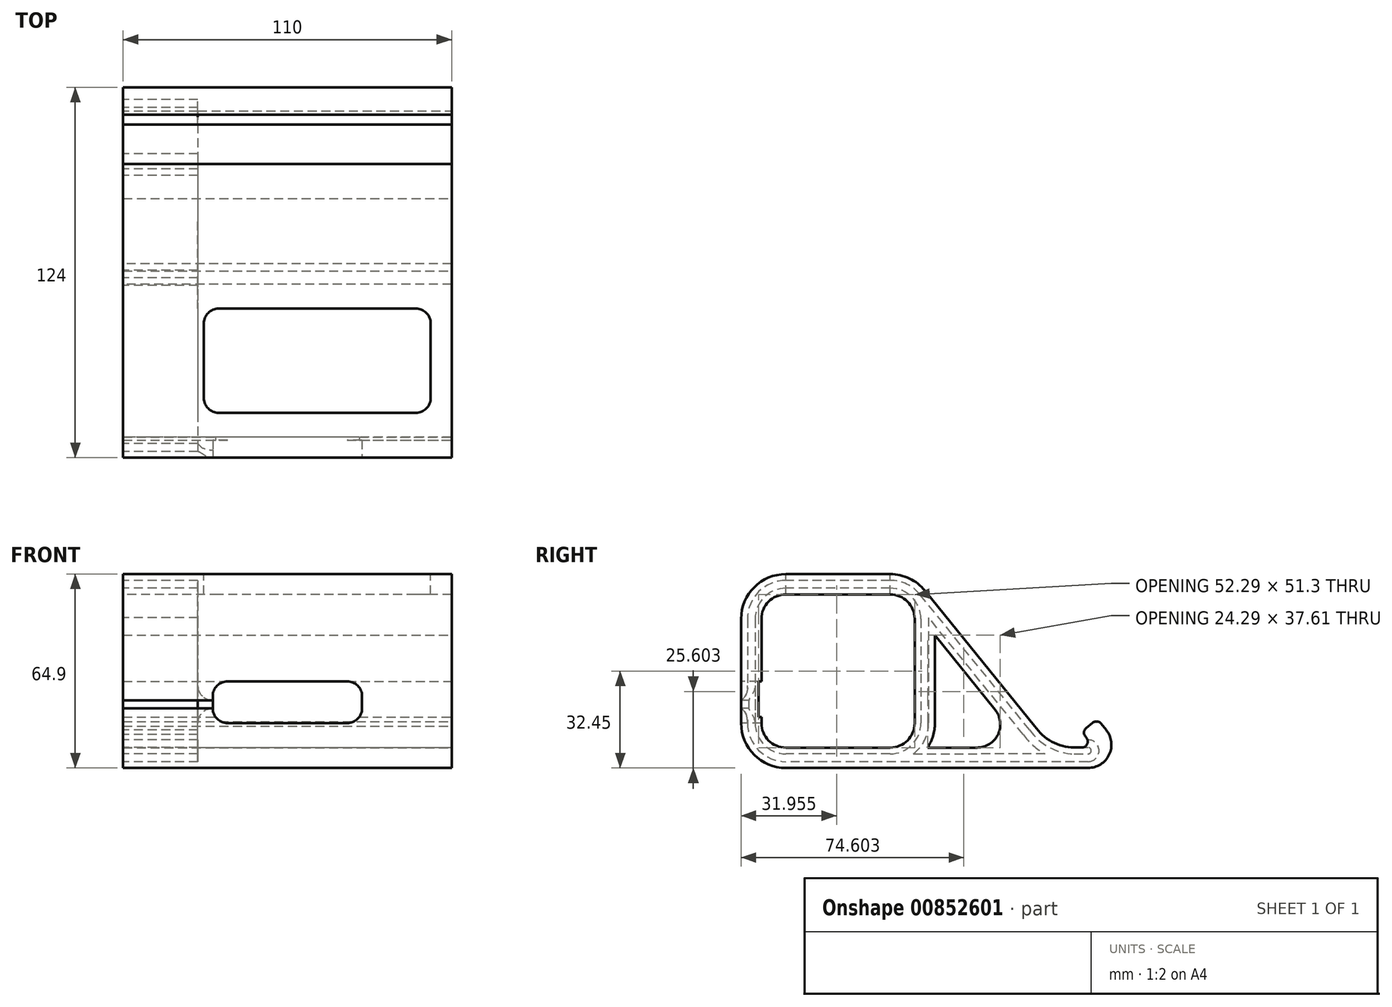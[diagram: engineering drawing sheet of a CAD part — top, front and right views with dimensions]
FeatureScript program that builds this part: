
annotation { "Feature Type Name" : "Feature", "Feature Type Description" : "" }
export const myFeature = defineFeature(function(context is Context, id is Id, definition is map)
    precondition{}
    {
        {
            var Q0;
            Q0=qCreatedBy(makeId("Right.planeOp"),FACE);
            var sketch = newSketch(context, id + "F0", { "sketchPlane" : qUnion([Q0])});
            skPoint(sketch, "E0.middle", {"position": v(0, 0) * mm});
            skArc(sketch, "E1.0", {"start": v(25.65, 17.45) * mm, "mid": v(23.25, 23.25) * mm, "end": v(17.45, 25.65) * mm});
            skLineSegment(sketch, "E1.1", {"start": v(25.65, 17.45) * mm, "end": v(25.65, -17.45) * mm});
            skLineSegment(sketch, "E1.2", {"start": v(17.45, 25.65) * mm, "end": v(-17.45, 25.65) * mm});
            skArc(sketch, "E1.3", {"start": v(17.45, -25.65) * mm, "mid": v(23.25, -23.25) * mm, "end": v(25.65, -17.45) * mm});
            skArc(sketch, "E1.4", {"start": v(-17.45, 25.65) * mm, "mid": v(-23.25, 23.25) * mm, "end": v(-25.65, 17.45) * mm});
            skLineSegment(sketch, "E1.5", {"start": v(-25.65, 17.45) * mm, "end": v(-25.65, -17.45) * mm});
            skArc(sketch, "E1.6", {"start": v(-25.65, -17.45) * mm, "mid": v(-23.25, -23.25) * mm, "end": v(-17.45, -25.65) * mm});
            skLineSegment(sketch, "E1.7", {"start": v(17.45, -25.65) * mm, "end": v(-17.45, -25.65) * mm});
            skLineSegment(sketch, "E2.0", {"start": v(-32.45, 17.45) * mm, "end": v(-32.45, -17.45) * mm});
            skArc(sketch, "E2.1", {"start": v(-17.45, 32.45) * mm, "mid": v(-28.06, 28.06) * mm, "end": v(-32.45, 17.45) * mm});
            skArc(sketch, "E2.2", {"start": v(-32.45, -17.45) * mm, "mid": v(-28.06, -28.06) * mm, "end": v(-17.45, -32.45) * mm});
            skLineSegment(sketch, "E2.3", {"start": v(17.45, 32.45) * mm, "end": v(-17.45, 32.45) * mm});
            skLineSegment(sketch, "E2.4", {"start": v(17.45, -32.45) * mm, "end": v(-17.45, -32.45) * mm});
            skArc(sketch, "E2.5", {"start": v(17.45, -32.45) * mm, "mid": v(28.06, -28.06) * mm, "end": v(32.45, -17.45) * mm});
            skLineSegment(sketch, "E2.6", {"start": v(32.45, 17.45) * mm, "end": v(32.45, -17.45) * mm});
            skArc(sketch, "E2.7", {"start": v(32.45, 17.45) * mm, "mid": v(28.06, 28.06) * mm, "end": v(17.45, 32.45) * mm});
            skLineSegment(sketch, "E3.0", {"start": v(17.45, -27.75) * mm, "end": v(-17.45, -27.75) * mm});
            skArc(sketch, "E3.1", {"start": v(-27.75, -17.45) * mm, "mid": v(-24.73, -24.73) * mm, "end": v(-17.45, -27.75) * mm});
            skArc(sketch, "E3.2", {"start": v(17.45, -27.75) * mm, "mid": v(24.73, -24.73) * mm, "end": v(27.75, -17.45) * mm});
            skLineSegment(sketch, "E3.3", {"start": v(-27.75, 17.45) * mm, "end": v(-27.75, -17.45) * mm});
            skLineSegment(sketch, "E3.4", {"start": v(27.75, 17.45) * mm, "end": v(27.75, -17.45) * mm});
            skArc(sketch, "E3.5", {"start": v(27.75, 17.45) * mm, "mid": v(24.73, 24.73) * mm, "end": v(17.45, 27.75) * mm});
            skLineSegment(sketch, "E3.6", {"start": v(17.45, 27.75) * mm, "end": v(-17.45, 27.75) * mm});
            skArc(sketch, "E3.7", {"start": v(-17.45, 27.75) * mm, "mid": v(-24.73, 24.73) * mm, "end": v(-27.75, 17.45) * mm});
            skArc(sketch, "E4.0", {"start": v(30.35, 17.45) * mm, "mid": v(26.57, 26.57) * mm, "end": v(17.45, 30.35) * mm});
            skLineSegment(sketch, "E4.1", {"start": v(30.35, 17.45) * mm, "end": v(30.35, -17.45) * mm});
            skLineSegment(sketch, "E4.2", {"start": v(17.45, 30.35) * mm, "end": v(-17.45, 30.35) * mm});
            skArc(sketch, "E4.3", {"start": v(17.45, -30.35) * mm, "mid": v(26.57, -26.57) * mm, "end": v(30.35, -17.45) * mm});
            skArc(sketch, "E4.4", {"start": v(-17.45, 30.35) * mm, "mid": v(-26.57, 26.57) * mm, "end": v(-30.35, 17.45) * mm});
            skLineSegment(sketch, "E4.5", {"start": v(-30.35, 17.45) * mm, "end": v(-30.35, -17.45) * mm});
            skArc(sketch, "E4.6", {"start": v(-30.35, -17.45) * mm, "mid": v(-26.57, -26.57) * mm, "end": v(-17.45, -30.35) * mm});
            skLineSegment(sketch, "E4.7", {"start": v(17.45, -30.35) * mm, "end": v(-17.45, -30.35) * mm});
            skSolve(sketch);
        }
        {
            var Q0;
            Q0=makeQuery(id+"F0.imprint","IMPRINT",FACE,{"disambiguationData":[TD([[makeQuery(id+"F0.imprint","IMPRINT",EDGE,{"derivedFrom":sQuery(id+"F0.wireOp",EDGE,"E3.0")}),1.0]])]});
            var Q1;
            Q1=makeQuery(id+"F0.imprint","IMPRINT",FACE,{"disambiguationData":[TD([[makeQuery(id+"F0.imprint","IMPRINT",EDGE,{"derivedFrom":sQuery(id+"F0.wireOp",EDGE,"E1.0")}),-1.0]])]});
            var Q2;
            Q2=makeQuery(id+"F0.imprint","IMPRINT",FACE,{"disambiguationData":[TD([[makeQuery(id+"F0.imprint","IMPRINT",EDGE,{"derivedFrom":sQuery(id+"F0.wireOp",EDGE,"E2.0")}),1.0]])]});
            extrude(context, id + "F1", {"entities" : qUnion([Q0, Q1, Q2]), "endBound" : BoundingType.SYMMETRIC, "depth" : 110 * mm, "offsetDistance" : 25 * mm});
        }
        {
            var Q0;
            Q0=makeQuery(id+"F1.opExtrude","SWEPT_FACE",FACE,{"disambiguationData":[OSD([sQuery(id+"F0.wireOp",EDGE,"E2.0")])]});
            var sketch = newSketch(context, id + "F2", { "sketchPlane" : qUnion([Q0])});
            skLineSegment(sketch, "E5", {"start": v(-55, -4.86) * mm, "end": v(-25, -4.86) * mm, "construction": true});
            skLineSegment(sketch, "E6", {"start": v(55, -5.4) * mm, "end": v(25, -5.4) * mm, "construction": true});
            skLineSegment(sketch, "E7", {"start": v(0, -17.45) * mm, "end": v(0, -3.45) * mm, "construction": true});
            skLineSegment(sketch, "E8.bottom", {"start": v(-25, -17.45) * mm, "end": v(25, -17.45) * mm});
            skLineSegment(sketch, "E8.top", {"start": v(-25, -3.45) * mm, "end": v(25, -3.45) * mm});
            skLineSegment(sketch, "E8.left", {"start": v(-25, -17.45) * mm, "end": v(-25, -3.45) * mm});
            skLineSegment(sketch, "E8.right", {"start": v(25, -17.45) * mm, "end": v(25, -3.45) * mm});
            skSolve(sketch);
        }
        {
            var Q0;
            Q0=makeQuery(id+"F2.imprint","IMPRINT",FACE,{"disambiguationData":[TD([[makeQuery(id+"F2.imprint","IMPRINT",EDGE,{"derivedFrom":sQuery(id+"F2.wireOp",EDGE,"E8.bottom")}),-1.0]])]});
            extrude(context, id + "F3", {"entities" : qUnion([Q0]), "operationType" : NewBodyOperationType.REMOVE, "oppositeDirection" : true, "depth" : 7 * mm, "offsetDistance" : 25 * mm});
        }
        {
            var Q0;
            Q0=makeQuery(id+"F1.opExtrude","CAP_FACE",FACE,{"disambiguationData":[OSD([sQuery(id+"F0.wireOp",EDGE,"E1.0"),sQuery(id+"F0.wireOp",EDGE,"E1.1"),sQuery(id+"F0.wireOp",EDGE,"E1.2"),sQuery(id+"F0.wireOp",EDGE,"E1.3"),sQuery(id+"F0.wireOp",EDGE,"E1.4"),sQuery(id+"F0.wireOp",EDGE,"E1.5"),sQuery(id+"F0.wireOp",EDGE,"E1.6"),sQuery(id+"F0.wireOp",EDGE,"E1.7"),sQuery(id+"F0.wireOp",EDGE,"E2.0"),sQuery(id+"F0.wireOp",EDGE,"E2.1"),sQuery(id+"F0.wireOp",EDGE,"E2.2"),sQuery(id+"F0.wireOp",EDGE,"E2.3"),sQuery(id+"F0.wireOp",EDGE,"E2.4"),sQuery(id+"F0.wireOp",EDGE,"E2.5"),sQuery(id+"F0.wireOp",EDGE,"E2.6"),sQuery(id+"F0.wireOp",EDGE,"E2.7")])],"isStart":false});
            var sketch = newSketch(context, id + "F4", { "sketchPlane" : qUnion([Q0])});
            skLineSegment(sketch, "E9", {"start": v(-29.91, -17.45) * mm, "end": v(-25.65, -17.45) * mm, "construction": true});
            skLineSegment(sketch, "E10", {"start": v(-27.78, -17.45) * mm, "end": v(-27.78, -3.45) * mm, "construction": true});
            skLineSegment(sketch, "E11.bottom", {"start": v(-25.64, -3.45) * mm, "end": v(-26.64, -3.45) * mm});
            skLineSegment(sketch, "E11.top", {"start": v(-25.64, -15.45) * mm, "end": v(-26.64, -15.45) * mm});
            skLineSegment(sketch, "E11.left", {"start": v(-25.64, -3.45) * mm, "end": v(-25.64, -15.45) * mm});
            skLineSegment(sketch, "E11.right", {"start": v(-26.64, -3.45) * mm, "end": v(-26.64, -15.45) * mm});
            skSolve(sketch);
        }
        {
            var Q0;
            {var subQ0=sQuery(id+"F4.wireOp",EDGE,"E11.right");Q0=makeQuery(id+"F4.imprint","IMPRINT",FACE,{"disambiguationData":[TD([[makeQuery(id+"F4.imprint","IMPRINT",EDGE,{"derivedFrom":subQ0}),1.0]])]});}
            extrude(context, id + "F5", {"entities" : qUnion([Q0]), "operationType" : NewBodyOperationType.REMOVE, "oppositeDirection" : true, "depth" : 110 * mm, "offsetDistance" : 25 * mm});
        }
        {
            var Q0;
            Q0=makeQuery(id+"F1.opExtrude","CAP_FACE",FACE,{"disambiguationData":[OSD([sQuery(id+"F0.wireOp",EDGE,"E1.0"),sQuery(id+"F0.wireOp",EDGE,"E1.1"),sQuery(id+"F0.wireOp",EDGE,"E1.2"),sQuery(id+"F0.wireOp",EDGE,"E1.3"),sQuery(id+"F0.wireOp",EDGE,"E1.4"),sQuery(id+"F0.wireOp",EDGE,"E1.5"),sQuery(id+"F0.wireOp",EDGE,"E1.6"),sQuery(id+"F0.wireOp",EDGE,"E1.7"),sQuery(id+"F0.wireOp",EDGE,"E2.0"),sQuery(id+"F0.wireOp",EDGE,"E2.1"),sQuery(id+"F0.wireOp",EDGE,"E2.2"),sQuery(id+"F0.wireOp",EDGE,"E2.3"),sQuery(id+"F0.wireOp",EDGE,"E2.4"),sQuery(id+"F0.wireOp",EDGE,"E2.5"),sQuery(id+"F0.wireOp",EDGE,"E2.6"),sQuery(id+"F0.wireOp",EDGE,"E2.7")])],"isStart":false});
            var sketch = newSketch(context, id + "F6", { "sketchPlane" : qUnion([Q0])});
            skLineSegment(sketch, "E12", {"start": v(67.38, -20.37) * mm, "end": v(28.06, 28.19) * mm});
            skPoint(sketch, "E12.endSnap0", {"position": v(28.06, 28.06) * mm});
            skPoint(sketch, "E13.end.orphan", {"position": v(36.97, -25.63) * mm});
            skLineSegment(sketch, "E14", {"start": v(0, -32.45) * mm, "end": v(77.16, -32.45) * mm});
            skLineSegment(sketch, "E15", {"start": v(71.64, -25.63) * mm, "end": v(71.65, -25.65) * mm});
            skLineSegment(sketch, "E16.0", {"start": v(52.61, -12.94) * mm, "end": v(22.77, 23.9) * mm});
            skLineSegment(sketch, "E16.1", {"start": v(0, -25.65) * mm, "end": v(46.55, -25.65) * mm});
            skArc(sketch, "E17.filletArc", {"start": v(46.55, -25.65) * mm, "mid": v(53.6, -21.2) * mm, "end": v(52.61, -12.94) * mm});
            skLineSegment(sketch, "E18", {"start": v(79.1, -25.63) * mm, "end": v(81.64, -25.63) * mm});
            skLineSegment(sketch, "E19", {"start": v(83.2, -22.37) * mm, "end": v(82.81, -21.9) * mm});
            skLineSegment(sketch, "E20", {"start": v(83.1, -19.09) * mm, "end": v(85.28, -17.33) * mm});
            skLineSegment(sketch, "E21", {"start": v(88.1, -17.62) * mm, "end": v(89.81, -19.74) * mm});
            skLineSegment(sketch, "E22", {"start": v(81.35, -32.45) * mm, "end": v(83.75, -32.45) * mm});
            skArc(sketch, "E23.filletArc", {"start": v(83.75, -32.45) * mm, "mid": v(90.79, -28) * mm, "end": v(89.81, -19.74) * mm});
            skPoint(sketch, "E24.visualSharp", {"position": v(86.84, -16.07) * mm});
            skArc(sketch, "E24.filletArc", {"start": v(88.1, -17.62) * mm, "mid": v(86.75, -16.9) * mm, "end": v(85.28, -17.33) * mm});
            skPoint(sketch, "E25.visualSharp", {"position": v(81.55, -20.35) * mm});
            skArc(sketch, "E25.filletArc", {"start": v(83.1, -19.09) * mm, "mid": v(82.38, -20.43) * mm, "end": v(82.81, -21.9) * mm});
            skPoint(sketch, "E26.visualSharp", {"position": v(85.83, -25.63) * mm});
            skArc(sketch, "E26.filletArc", {"start": v(81.64, -25.63) * mm, "mid": v(83.44, -24.5) * mm, "end": v(83.2, -22.37) * mm});
            skLineSegment(sketch, "E27", {"start": v(77.16, -32.45) * mm, "end": v(81.35, -32.45) * mm});
            skArc(sketch, "E28", {"start": v(65.83, -18.46) * mm, "mid": v(71.62, -23.63) * mm, "end": v(79.1, -25.63) * mm});
            skSolve(sketch);
        }
        {
            var Q0;
            {var subQ1=sQuery(id+"F6.wireOp",EDGE,"E17.filletArc");Q0=makeQuery(id+"F6.imprint","IMPRINT",FACE,{"disambiguationData":[TD([[makeQuery(id+"F6.imprint","IMPRINT",EDGE,{"derivedFrom":subQ1}),-1.0]])]});}
            extrude(context, id + "F7", {"entities" : qUnion([Q0]), "oppositeDirection" : true, "depth" : 110 * mm, "offsetDistance" : 25 * mm});
        }
        {
            var Q0;
            Q0=makeQuery(id+"F1.opExtrude","SWEPT_BODY",BODY,{"disambiguationData":[OSD([sQuery(id+"F0.wireOp",EDGE,"E1.0"),sQuery(id+"F0.wireOp",EDGE,"E1.1"),sQuery(id+"F0.wireOp",EDGE,"E1.2"),sQuery(id+"F0.wireOp",EDGE,"E1.3"),sQuery(id+"F0.wireOp",EDGE,"E1.4"),sQuery(id+"F0.wireOp",EDGE,"E1.5"),sQuery(id+"F0.wireOp",EDGE,"E1.6"),sQuery(id+"F0.wireOp",EDGE,"E1.7"),sQuery(id+"F0.wireOp",EDGE,"E2.0"),sQuery(id+"F0.wireOp",EDGE,"E2.1"),sQuery(id+"F0.wireOp",EDGE,"E2.2"),sQuery(id+"F0.wireOp",EDGE,"E2.3"),sQuery(id+"F0.wireOp",EDGE,"E2.4"),sQuery(id+"F0.wireOp",EDGE,"E2.5"),sQuery(id+"F0.wireOp",EDGE,"E2.6"),sQuery(id+"F0.wireOp",EDGE,"E2.7")])]});
            var Q1;
            Q1=makeQuery(id+"F7.opExtrude","SWEPT_BODY",BODY,{"disambiguationData":[OSD([sQuery(id+"F0.wireOp",EDGE,"E2.5"),sQuery(id+"F0.wireOp",EDGE,"E2.6"),sQuery(id+"F0.wireOp",EDGE,"E2.7"),sQuery(id+"F6.wireOp",EDGE,"E12"),sQuery(id+"F6.wireOp",EDGE,"E14"),sQuery(id+"F6.wireOp",EDGE,"E16.0"),sQuery(id+"F6.wireOp",EDGE,"E16.1"),sQuery(id+"F6.wireOp",EDGE,"E17.filletArc"),sQuery(id+"F6.wireOp",EDGE,"E18"),sQuery(id+"F6.wireOp",EDGE,"E19"),sQuery(id+"F6.wireOp",EDGE,"E20"),sQuery(id+"F6.wireOp",EDGE,"E21"),sQuery(id+"F6.wireOp",EDGE,"E22"),sQuery(id+"F6.wireOp",EDGE,"E23.filletArc"),sQuery(id+"F6.wireOp",EDGE,"E24.filletArc"),sQuery(id+"F6.wireOp",EDGE,"E25.filletArc"),sQuery(id+"F6.wireOp",EDGE,"E26.filletArc"),sQuery(id+"F6.wireOp",EDGE,"E27"),sQuery(id+"F6.wireOp",EDGE,"E28")])]});
            booleanBodies(context, id + "F8", {"operationType" : BooleanOperationType.UNION, "tools" : qUnion([Q0, Q1])});
        }
        {
            var Q0;
            Q0=makeQuery(id+"F3.boolean.opBoolean","COPY",EDGE,{"derivedFrom":makeQuery(id+"F3.opExtrude","SWEPT_EDGE",EDGE,{"disambiguationData":[OSD([sQuery(id+"F0.wireOp",EDGE,"E2.0"),sQuery(id+"F0.wireOp",EDGE,"E2.2"),sQuery(id+"F2.wireOp",EDGE,"E8.bottom"),sQuery(id+"F2.wireOp",EDGE,"E8.left")])]})});
            var Q1;
            Q1=makeQuery(id+"F3.boolean.opBoolean","COPY",EDGE,{"derivedFrom":makeQuery(id+"F3.opExtrude","SWEPT_EDGE",EDGE,{"disambiguationData":[OSD([sQuery(id+"F2.wireOp",EDGE,"E8.top"),sQuery(id+"F2.wireOp",EDGE,"E8.left")])]})});
            var Q2;
            Q2=makeQuery(id+"F3.boolean.opBoolean","COPY",EDGE,{"derivedFrom":makeQuery(id+"F3.opExtrude","SWEPT_EDGE",EDGE,{"disambiguationData":[OSD([sQuery(id+"F2.wireOp",EDGE,"E8.top"),sQuery(id+"F2.wireOp",EDGE,"E8.right")])]})});
            var Q3;
            Q3=makeQuery(id+"F3.boolean.opBoolean","COPY",EDGE,{"derivedFrom":makeQuery(id+"F3.opExtrude","SWEPT_EDGE",EDGE,{"disambiguationData":[OSD([sQuery(id+"F0.wireOp",EDGE,"E2.0"),sQuery(id+"F0.wireOp",EDGE,"E2.2"),sQuery(id+"F2.wireOp",EDGE,"E8.bottom"),sQuery(id+"F2.wireOp",EDGE,"E8.right")])]})});
            fillet(context, id + "F9", {"entities" : qUnion([Q0, Q1, Q2, Q3]), "radius" : 5 * mm, "tangentPropagation" : true, "allowEdgeOverflow" : false});
        }
        {
            var Q0;
            {var subQ0=sQuery(id+"F0.wireOp",EDGE,"E2.7");var subQ1=sQuery(id+"F0.wireOp",EDGE,"E2.6");var subQ2=sQuery(id+"F0.wireOp",EDGE,"E2.5");Q0=makeQuery(id+"F8.opBoolean","MERGE",FACE,{"derivedFrom":[makeQuery(id+"F1.opExtrude","CAP_FACE",FACE,{"disambiguationData":[OSD([sQuery(id+"F0.wireOp",EDGE,"E1.0"),sQuery(id+"F0.wireOp",EDGE,"E1.1"),sQuery(id+"F0.wireOp",EDGE,"E1.2"),sQuery(id+"F0.wireOp",EDGE,"E1.3"),sQuery(id+"F0.wireOp",EDGE,"E1.4"),sQuery(id+"F0.wireOp",EDGE,"E1.5"),sQuery(id+"F0.wireOp",EDGE,"E1.6"),sQuery(id+"F0.wireOp",EDGE,"E1.7"),sQuery(id+"F0.wireOp",EDGE,"E2.0"),sQuery(id+"F0.wireOp",EDGE,"E2.1"),sQuery(id+"F0.wireOp",EDGE,"E2.2"),sQuery(id+"F0.wireOp",EDGE,"E2.3"),sQuery(id+"F0.wireOp",EDGE,"E2.4"),subQ2,subQ1,subQ0])],"isStart":true}),makeQuery(id+"F7.opExtrude","CAP_FACE",FACE,{"disambiguationData":[OSD([subQ2,subQ1,subQ0,sQuery(id+"F6.wireOp",EDGE,"E12"),sQuery(id+"F6.wireOp",EDGE,"E14"),sQuery(id+"F6.wireOp",EDGE,"E16.0"),sQuery(id+"F6.wireOp",EDGE,"E16.1"),sQuery(id+"F6.wireOp",EDGE,"E17.filletArc"),sQuery(id+"F6.wireOp",EDGE,"E18"),sQuery(id+"F6.wireOp",EDGE,"E19"),sQuery(id+"F6.wireOp",EDGE,"E20"),sQuery(id+"F6.wireOp",EDGE,"E21"),sQuery(id+"F6.wireOp",EDGE,"E22"),sQuery(id+"F6.wireOp",EDGE,"E23.filletArc"),sQuery(id+"F6.wireOp",EDGE,"E24.filletArc"),sQuery(id+"F6.wireOp",EDGE,"E25.filletArc"),sQuery(id+"F6.wireOp",EDGE,"E26.filletArc"),sQuery(id+"F6.wireOp",EDGE,"E27"),sQuery(id+"F6.wireOp",EDGE,"E28")])],"isStart":false})]});}
            var sketch = newSketch(context, id + "F10", { "sketchPlane" : qUnion([Q0])});
            skLineSegment(sketch, "E29.0", {"start": v(27.75, 17.45) * mm, "end": v(27.75, -3.45) * mm});
            skArc(sketch, "E29.1", {"start": v(17.45, 27.75) * mm, "mid": v(24.73, 24.73) * mm, "end": v(27.75, 17.45) * mm});
            skLineSegment(sketch, "E29.2", {"start": v(-17.45, 27.75) * mm, "end": v(17.45, 27.75) * mm});
            skArc(sketch, "E29.3", {"start": v(-27.75, 17.45) * mm, "mid": v(-24.73, 24.73) * mm, "end": v(-17.45, 27.75) * mm});
            skLineSegment(sketch, "E29.4", {"start": v(-27.75, 17.45) * mm, "end": v(-27.75, -17.45) * mm});
            skLineSegment(sketch, "E29.5", {"start": v(27.75, -15.45) * mm, "end": v(27.75, -17.45) * mm});
            skArc(sketch, "E29.6", {"start": v(27.75, -17.45) * mm, "mid": v(24.73, -24.73) * mm, "end": v(17.45, -27.75) * mm});
            skLineSegment(sketch, "E29.7", {"start": v(-17.45, -27.75) * mm, "end": v(17.45, -27.75) * mm});
            skArc(sketch, "E29.8", {"start": v(-17.45, -27.75) * mm, "mid": v(-24.73, -24.73) * mm, "end": v(-27.75, -17.45) * mm});
            skLineSegment(sketch, "E30.0", {"start": v(-79.08, -27.73) * mm, "end": v(-81.64, -27.73) * mm});
            skArc(sketch, "E30.1", {"start": v(-64.15, -19.73) * mm, "mid": v(-70.67, -25.5) * mm, "end": v(-79.08, -27.73) * mm});
            skLineSegment(sketch, "E30.2", {"start": v(-64.15, -19.73) * mm, "end": v(-27.48, 25.57) * mm});
            skArc(sketch, "E30.3", {"start": v(-27.48, 25.57) * mm, "mid": v(-23, 29.1) * mm, "end": v(-17.45, 30.35) * mm});
            skLineSegment(sketch, "E30.4", {"start": v(-17.45, 30.35) * mm, "end": v(17.45, 30.35) * mm});
            skLineSegment(sketch, "E30.5", {"start": v(-83.75, -30.35) * mm, "end": v(17.45, -30.35) * mm});
            skArc(sketch, "E30.6", {"start": v(30.35, -17.45) * mm, "mid": v(26.57, -26.57) * mm, "end": v(17.45, -30.35) * mm});
            skLineSegment(sketch, "E30.7", {"start": v(30.35, 17.45) * mm, "end": v(30.35, -17.45) * mm});
            skArc(sketch, "E30.8", {"start": v(17.45, 30.35) * mm, "mid": v(26.57, 26.57) * mm, "end": v(30.35, 17.45) * mm});
            skLineSegment(sketch, "E31", {"start": v(27.75, -3.45) * mm, "end": v(27.75, -15.45) * mm});
            skLineSegment(sketch, "E32.0", {"start": v(-30.35, 17.89) * mm, "end": v(-30.35, -17.45) * mm});
            skArc(sketch, "E32.2", {"start": v(-25.22, -27.75) * mm, "mid": v(-29, -23.2) * mm, "end": v(-30.35, -17.45) * mm});
            skLineSegment(sketch, "E32.3", {"start": v(-25.22, -27.75) * mm, "end": v(-46.55, -27.75) * mm});
            skArc(sketch, "E32.4", {"start": v(-46.55, -27.75) * mm, "mid": v(-46.55, -27.75) * mm, "end": v(-46.56, -27.75) * mm});
            skLineSegment(sketch, "E33", {"start": v(-69.33, -27.74) * mm, "end": v(-46.55, -27.75) * mm});
            skLineSegment(sketch, "E34.0", {"start": v(-62.08, -21.3) * mm, "end": v(-30.35, 17.89) * mm});
            skArc(sketch, "E34.1", {"start": v(-62.08, -21.3) * mm, "mid": v(-65.33, -24.93) * mm, "end": v(-69.33, -27.74) * mm});
            skLineSegment(sketch, "E35", {"start": v(-81.64, -27.73) * mm, "end": v(-83.75, -27.73) * mm});
            skLineSegment(sketch, "E36", {"start": v(-81.64, -25.63) * mm, "end": v(-83.75, -25.63) * mm});
            skLineSegment(sketch, "E37", {"start": v(-83.75, -23.03) * mm, "end": v(-83.55, -23.03) * mm});
            skArc(sketch, "E38", {"start": v(-83.75, -25.63) * mm, "mid": v(-84.8, -26.68) * mm, "end": v(-83.75, -27.73) * mm});
            skArc(sketch, "E39", {"start": v(-83.75, -23.03) * mm, "mid": v(-87.4, -26.7) * mm, "end": v(-83.75, -30.35) * mm});
            skSolve(sketch);
        }
        {
            var Q0;
            Q0=makeQuery(id+"F10.imprint","IMPRINT",FACE,{"disambiguationData":[TD([[makeQuery(id+"F10.imprint","IMPRINT",EDGE,{"derivedFrom":sQuery(id+"F10.wireOp",EDGE,"E29.0")}),1.0]])]});
            extrude(context, id + "F11", {"entities" : qUnion([Q0]), "operationType" : NewBodyOperationType.REMOVE, "oppositeDirection" : true, "depth" : 25 * mm, "offsetDistance" : 25 * mm});
        }
        {
            var Q0;
            Q0=makeQuery(id+"F1.opExtrude","SWEPT_FACE",FACE,{"disambiguationData":[OSD([sQuery(id+"F0.wireOp",EDGE,"E2.0")])]});
            var sketch = newSketch(context, id + "F12", { "sketchPlane" : qUnion([Q0])});
            skLineSegment(sketch, "E40.bottom", {"start": v(-55.75, -9.85) * mm, "end": v(-25, -9.85) * mm});
            skLineSegment(sketch, "E40.top", {"start": v(-55.75, -12.45) * mm, "end": v(-25, -12.45) * mm});
            skLineSegment(sketch, "E40.left", {"start": v(-55.75, -9.85) * mm, "end": v(-55.75, -12.45) * mm});
            skLineSegment(sketch, "E40.right", {"start": v(-25, -9.85) * mm, "end": v(-25, -12.45) * mm});
            skSolve(sketch);
        }
        {
            var Q0;
            {var subQ0=sQuery(id+"F12.wireOp",EDGE,"E40.right");Q0=makeQuery(id+"F12.imprint","IMPRINT",FACE,{"disambiguationData":[TD([[makeQuery(id+"F12.imprint","IMPRINT",EDGE,{"derivedFrom":subQ0}),1.0]])]});}
            extrude(context, id + "F13", {"entities" : qUnion([Q0]), "operationType" : NewBodyOperationType.REMOVE, "oppositeDirection" : true, "depth" : 2.6 * mm, "offsetDistance" : 25 * mm});
        }
        {
            var Q0;
            Q0=makeQuery(id+"F13.boolean.opBoolean","INTERSECT",EDGE,{"derivedFrom":[makeQuery(id+"F11.boolean.opBoolean","COPY",FACE,{"derivedFrom":makeQuery(id+"F11.opExtrude","SWEPT_FACE",FACE,{"disambiguationData":[OSD([sQuery(id+"F10.wireOp",EDGE,"E30.7")])]})}),makeQuery(id+"F13.opExtrude","SWEPT_FACE",FACE,{"disambiguationData":[OSD([sQuery(id+"F12.wireOp",EDGE,"E40.top")])]})]});
            var Q1;
            Q1=makeQuery(id+"F13.boolean.opBoolean","INTERSECT",EDGE,{"derivedFrom":[makeQuery(id+"F11.boolean.opBoolean","COPY",FACE,{"derivedFrom":makeQuery(id+"F11.opExtrude","SWEPT_FACE",FACE,{"disambiguationData":[OSD([sQuery(id+"F10.wireOp",EDGE,"E30.7")])]})}),makeQuery(id+"F13.opExtrude","SWEPT_FACE",FACE,{"disambiguationData":[OSD([sQuery(id+"F12.wireOp",EDGE,"E40.bottom")])]})]});
            fillet(context, id + "F14", {"entities" : qUnion([Q0, Q1]), "radius" : 5 * mm, "tangentPropagation" : true, "allowEdgeOverflow" : false});
        }
        {
            var Q0;
            Q0=makeQuery(id+"F13.boolean.opBoolean","INTERSECT",EDGE,{"derivedFrom":[makeQuery(id+"F11.boolean.opBoolean","COPY",FACE,{"derivedFrom":makeQuery(id+"F11.opExtrude","CAP_FACE",FACE,{"disambiguationData":[OSD([sQuery(id+"F6.wireOp",EDGE,"E26.filletArc"),sQuery(id+"F10.wireOp",EDGE,"E29.0"),sQuery(id+"F10.wireOp",EDGE,"E29.1"),sQuery(id+"F10.wireOp",EDGE,"E29.2"),sQuery(id+"F10.wireOp",EDGE,"E29.3"),sQuery(id+"F10.wireOp",EDGE,"E29.4"),sQuery(id+"F10.wireOp",EDGE,"E29.5"),sQuery(id+"F10.wireOp",EDGE,"E29.6"),sQuery(id+"F10.wireOp",EDGE,"E29.7"),sQuery(id+"F10.wireOp",EDGE,"E29.8"),sQuery(id+"F10.wireOp",EDGE,"E30.0"),sQuery(id+"F10.wireOp",EDGE,"E30.1"),sQuery(id+"F10.wireOp",EDGE,"E30.2"),sQuery(id+"F10.wireOp",EDGE,"E30.3"),sQuery(id+"F10.wireOp",EDGE,"E30.4"),sQuery(id+"F10.wireOp",EDGE,"E30.5"),sQuery(id+"F10.wireOp",EDGE,"E30.6"),sQuery(id+"F10.wireOp",EDGE,"E30.7"),sQuery(id+"F10.wireOp",EDGE,"E30.8"),sQuery(id+"F10.wireOp",EDGE,"E31"),sQuery(id+"F10.wireOp",EDGE,"E32.0"),sQuery(id+"F10.wireOp",EDGE,"E32.2"),sQuery(id+"F10.wireOp",EDGE,"E32.3"),sQuery(id+"F10.wireOp",EDGE,"E33"),sQuery(id+"F10.wireOp",EDGE,"E34.0"),sQuery(id+"F10.wireOp",EDGE,"E34.1"),sQuery(id+"F10.wireOp",EDGE,"E35"),sQuery(id+"F10.wireOp",EDGE,"E36"),sQuery(id+"F10.wireOp",EDGE,"E37"),sQuery(id+"F10.wireOp",EDGE,"E38"),sQuery(id+"F10.wireOp",EDGE,"E39")])],"isStart":false})}),makeQuery(id+"F13.opExtrude","SWEPT_FACE",FACE,{"disambiguationData":[OSD([sQuery(id+"F12.wireOp",EDGE,"E40.bottom")])]})]});
            var Q1;
            Q1=makeQuery(id+"F13.boolean.opBoolean","INTERSECT",EDGE,{"derivedFrom":[makeQuery(id+"F11.boolean.opBoolean","COPY",FACE,{"derivedFrom":makeQuery(id+"F11.opExtrude","CAP_FACE",FACE,{"disambiguationData":[OSD([sQuery(id+"F6.wireOp",EDGE,"E26.filletArc"),sQuery(id+"F10.wireOp",EDGE,"E29.0"),sQuery(id+"F10.wireOp",EDGE,"E29.1"),sQuery(id+"F10.wireOp",EDGE,"E29.2"),sQuery(id+"F10.wireOp",EDGE,"E29.3"),sQuery(id+"F10.wireOp",EDGE,"E29.4"),sQuery(id+"F10.wireOp",EDGE,"E29.5"),sQuery(id+"F10.wireOp",EDGE,"E29.6"),sQuery(id+"F10.wireOp",EDGE,"E29.7"),sQuery(id+"F10.wireOp",EDGE,"E29.8"),sQuery(id+"F10.wireOp",EDGE,"E30.0"),sQuery(id+"F10.wireOp",EDGE,"E30.1"),sQuery(id+"F10.wireOp",EDGE,"E30.2"),sQuery(id+"F10.wireOp",EDGE,"E30.3"),sQuery(id+"F10.wireOp",EDGE,"E30.4"),sQuery(id+"F10.wireOp",EDGE,"E30.5"),sQuery(id+"F10.wireOp",EDGE,"E30.6"),sQuery(id+"F10.wireOp",EDGE,"E30.7"),sQuery(id+"F10.wireOp",EDGE,"E30.8"),sQuery(id+"F10.wireOp",EDGE,"E31"),sQuery(id+"F10.wireOp",EDGE,"E32.0"),sQuery(id+"F10.wireOp",EDGE,"E32.2"),sQuery(id+"F10.wireOp",EDGE,"E32.3"),sQuery(id+"F10.wireOp",EDGE,"E33"),sQuery(id+"F10.wireOp",EDGE,"E34.0"),sQuery(id+"F10.wireOp",EDGE,"E34.1"),sQuery(id+"F10.wireOp",EDGE,"E35"),sQuery(id+"F10.wireOp",EDGE,"E36"),sQuery(id+"F10.wireOp",EDGE,"E37"),sQuery(id+"F10.wireOp",EDGE,"E38"),sQuery(id+"F10.wireOp",EDGE,"E39")])],"isStart":false})}),makeQuery(id+"F13.opExtrude","CAP_FACE",FACE,{"disambiguationData":[OSD([sQuery(id+"F0.wireOp",EDGE,"E2.0"),sQuery(id+"F12.wireOp",EDGE,"E40.bottom"),sQuery(id+"F12.wireOp",EDGE,"E40.top"),sQuery(id+"F12.wireOp",EDGE,"E40.right")])],"isStart":false})]});
            var Q2;
            Q2=makeQuery(id+"F13.boolean.opBoolean","INTERSECT",EDGE,{"derivedFrom":[makeQuery(id+"F11.boolean.opBoolean","COPY",FACE,{"derivedFrom":makeQuery(id+"F11.opExtrude","CAP_FACE",FACE,{"disambiguationData":[OSD([sQuery(id+"F6.wireOp",EDGE,"E26.filletArc"),sQuery(id+"F10.wireOp",EDGE,"E29.0"),sQuery(id+"F10.wireOp",EDGE,"E29.1"),sQuery(id+"F10.wireOp",EDGE,"E29.2"),sQuery(id+"F10.wireOp",EDGE,"E29.3"),sQuery(id+"F10.wireOp",EDGE,"E29.4"),sQuery(id+"F10.wireOp",EDGE,"E29.5"),sQuery(id+"F10.wireOp",EDGE,"E29.6"),sQuery(id+"F10.wireOp",EDGE,"E29.7"),sQuery(id+"F10.wireOp",EDGE,"E29.8"),sQuery(id+"F10.wireOp",EDGE,"E30.0"),sQuery(id+"F10.wireOp",EDGE,"E30.1"),sQuery(id+"F10.wireOp",EDGE,"E30.2"),sQuery(id+"F10.wireOp",EDGE,"E30.3"),sQuery(id+"F10.wireOp",EDGE,"E30.4"),sQuery(id+"F10.wireOp",EDGE,"E30.5"),sQuery(id+"F10.wireOp",EDGE,"E30.6"),sQuery(id+"F10.wireOp",EDGE,"E30.7"),sQuery(id+"F10.wireOp",EDGE,"E30.8"),sQuery(id+"F10.wireOp",EDGE,"E31"),sQuery(id+"F10.wireOp",EDGE,"E32.0"),sQuery(id+"F10.wireOp",EDGE,"E32.2"),sQuery(id+"F10.wireOp",EDGE,"E32.3"),sQuery(id+"F10.wireOp",EDGE,"E33"),sQuery(id+"F10.wireOp",EDGE,"E34.0"),sQuery(id+"F10.wireOp",EDGE,"E34.1"),sQuery(id+"F10.wireOp",EDGE,"E35"),sQuery(id+"F10.wireOp",EDGE,"E36"),sQuery(id+"F10.wireOp",EDGE,"E37"),sQuery(id+"F10.wireOp",EDGE,"E38"),sQuery(id+"F10.wireOp",EDGE,"E39")])],"isStart":false})}),makeQuery(id+"F13.opExtrude","SWEPT_FACE",FACE,{"disambiguationData":[OSD([sQuery(id+"F12.wireOp",EDGE,"E40.top")])]})]});
            fillet(context, id + "F15", {"entities" : qUnion([Q0, Q1, Q2]), "radius" : 5 * mm, "tangentPropagation" : true, "allowEdgeOverflow" : false});
        }
        {
            var Q0;
            Q0=makeQuery(id+"F1.opExtrude","SWEPT_FACE",FACE,{"disambiguationData":[OSD([sQuery(id+"F0.wireOp",EDGE,"E2.3")])]});
            var sketch = newSketch(context, id + "F16", { "sketchPlane" : qUnion([Q0])});
            skPoint(sketch, "E41.middle", {"position": v(0, 0) * mm});
            skLineSegment(sketch, "E42", {"start": v(-55, 6.8) * mm, "end": v(-28, 6.8) * mm, "construction": true});
            skLineSegment(sketch, "E43", {"start": v(55, 6.8) * mm, "end": v(48, 6.8) * mm, "construction": true});
            skLineSegment(sketch, "E44.bottom", {"start": v(-28, 17.45) * mm, "end": v(48, 17.45) * mm});
            skLineSegment(sketch, "E44.top", {"start": v(-28, -17.45) * mm, "end": v(48, -17.45) * mm});
            skLineSegment(sketch, "E44.left", {"start": v(-28, 17.45) * mm, "end": v(-28, -17.45) * mm});
            skLineSegment(sketch, "E44.right", {"start": v(48, 17.45) * mm, "end": v(48, -17.45) * mm});
            skSolve(sketch);
        }
        {
            var Q0;
            Q0=makeQuery(id+"F16.imprint","IMPRINT",FACE,{"disambiguationData":[TD([[makeQuery(id+"F16.imprint","IMPRINT",EDGE,{"derivedFrom":sQuery(id+"F16.wireOp",EDGE,"E44.bottom")}),1.0]])]});
            extrude(context, id + "F17", {"entities" : qUnion([Q0]), "operationType" : NewBodyOperationType.REMOVE, "oppositeDirection" : true, "depth" : 8 * mm, "offsetDistance" : 25 * mm});
        }
        {
            var Q0;
            Q0=makeQuery(id+"F17.boolean.opBoolean","COPY",EDGE,{"derivedFrom":makeQuery(id+"F17.opExtrude","SWEPT_EDGE",EDGE,{"disambiguationData":[OSD([sQuery(id+"F0.wireOp",EDGE,"E2.3"),sQuery(id+"F0.wireOp",EDGE,"E2.7"),sQuery(id+"F16.wireOp",EDGE,"E44.bottom"),sQuery(id+"F16.wireOp",EDGE,"E44.left")])]})});
            var Q1;
            Q1=makeQuery(id+"F17.boolean.opBoolean","COPY",EDGE,{"derivedFrom":makeQuery(id+"F17.opExtrude","SWEPT_EDGE",EDGE,{"disambiguationData":[OSD([sQuery(id+"F0.wireOp",EDGE,"E2.3"),sQuery(id+"F0.wireOp",EDGE,"E2.7"),sQuery(id+"F16.wireOp",EDGE,"E44.bottom"),sQuery(id+"F16.wireOp",EDGE,"E44.right")])]})});
            var Q2;
            Q2=makeQuery(id+"F17.boolean.opBoolean","COPY",EDGE,{"derivedFrom":makeQuery(id+"F17.opExtrude","SWEPT_EDGE",EDGE,{"disambiguationData":[OSD([sQuery(id+"F0.wireOp",EDGE,"E2.1"),sQuery(id+"F0.wireOp",EDGE,"E2.3"),sQuery(id+"F16.wireOp",EDGE,"E44.top"),sQuery(id+"F16.wireOp",EDGE,"E44.right")])]})});
            var Q3;
            Q3=makeQuery(id+"F17.boolean.opBoolean","COPY",EDGE,{"derivedFrom":makeQuery(id+"F17.opExtrude","SWEPT_EDGE",EDGE,{"disambiguationData":[OSD([sQuery(id+"F0.wireOp",EDGE,"E2.1"),sQuery(id+"F0.wireOp",EDGE,"E2.3"),sQuery(id+"F16.wireOp",EDGE,"E44.top"),sQuery(id+"F16.wireOp",EDGE,"E44.left")])]})});
            fillet(context, id + "F18", {"entities" : qUnion([Q0, Q1, Q2, Q3]), "radius" : 5 * mm, "tangentPropagation" : true, "allowEdgeOverflow" : false});
        }
    });
